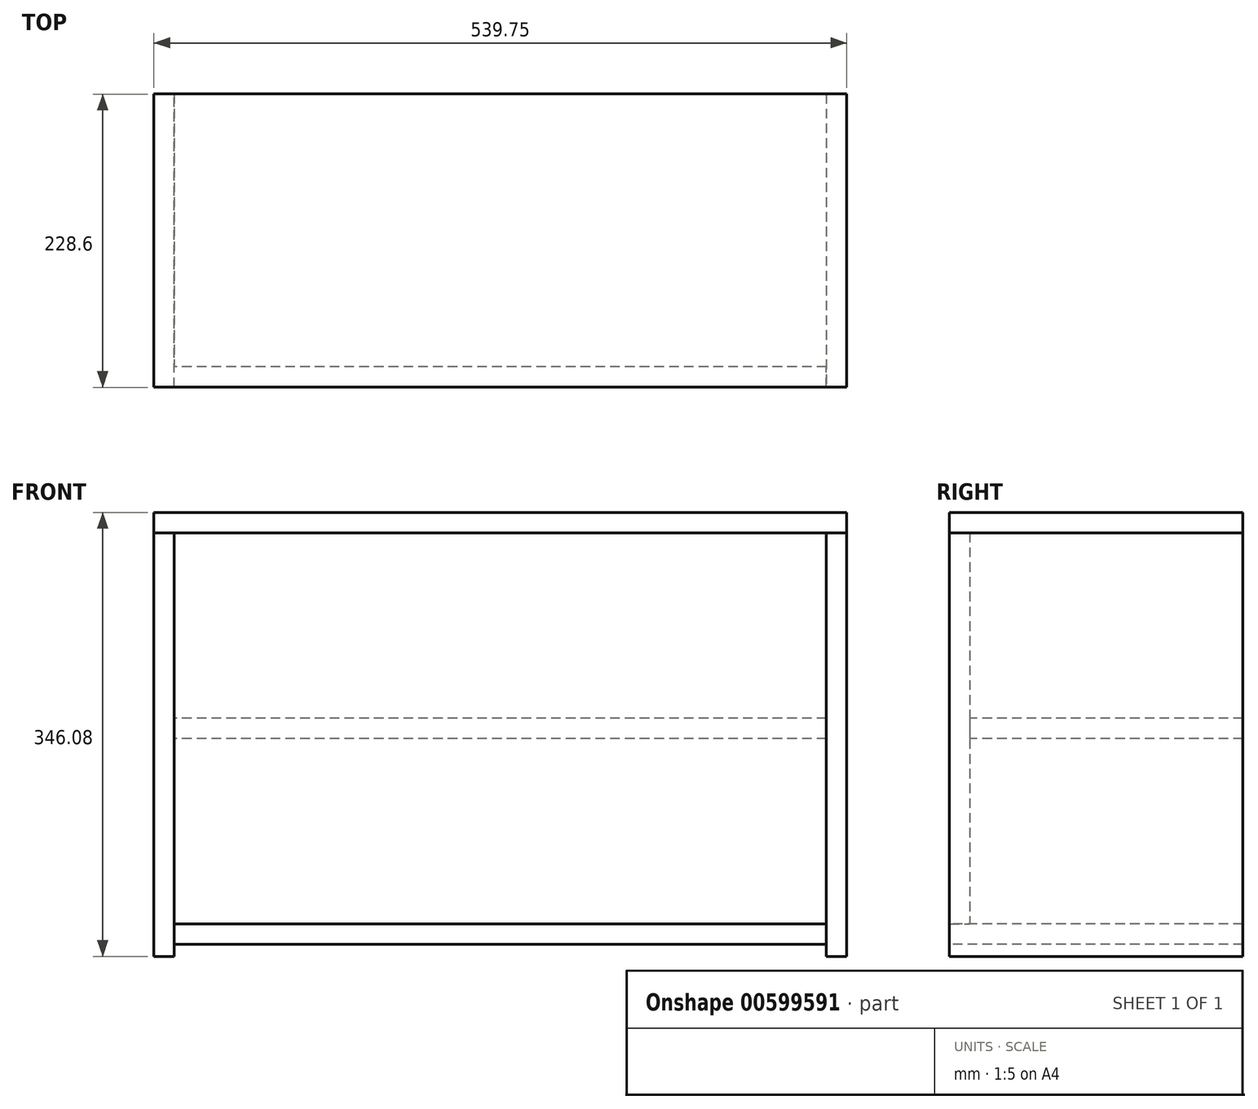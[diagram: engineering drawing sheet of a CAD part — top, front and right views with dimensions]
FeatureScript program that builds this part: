
annotation { "Feature Type Name" : "Feature", "Feature Type Description" : "" }
export const myFeature = defineFeature(function(context is Context, id is Id, definition is map)
    precondition{}
    {
        {
            var Q0;
            Q0=qCreatedBy(makeId("Front.planeOp"),FACE);
            var sketch = newSketch(context, id + "F0", { "sketchPlane" : qUnion([Q0])});
            skLineSegment(sketch, "E0.bottom", {"start": v(-62.15, 287.23) * mm, "end": v(445.85, 287.23) * mm});
            skLineSegment(sketch, "E0.top", {"start": v(-62.15, -17.57) * mm, "end": v(445.85, -17.57) * mm});
            skLineSegment(sketch, "E0.left", {"start": v(-62.15, 287.23) * mm, "end": v(-62.15, -17.57) * mm});
            skLineSegment(sketch, "E0.right", {"start": v(445.85, 287.23) * mm, "end": v(445.85, -17.57) * mm});
            skSolve(sketch);
        }
        {
            var Q0;
            Q0=makeQuery(id+"F0.imprint","IMPRINT",FACE,{"disambiguationData":[TD([[makeQuery(id+"F0.imprint","IMPRINT",EDGE,{"derivedFrom":sQuery(id+"F0.wireOp",EDGE,"E0.bottom")}),-1.0]])]});
            extrude(context, id + "F1", {"entities" : qUnion([Q0]), "depth" : 15.88 * mm, "offsetDistance" : 25.4 * mm});
        }
        {
            var Q0;
            Q0=makeQuery(id+"F1.opExtrude","SWEPT_FACE",FACE,{"disambiguationData":[OSD([sQuery(id+"F0.wireOp",EDGE,"E0.right")])]});
            var sketch = newSketch(context, id + "F2", { "sketchPlane" : qUnion([Q0])});
            skLineSegment(sketch, "E1.bottom", {"start": v(-15.88, 287.23) * mm, "end": v(212.73, 287.23) * mm});
            skLineSegment(sketch, "E1.top", {"start": v(-15.87, -42.97) * mm, "end": v(212.73, -42.97) * mm});
            skLineSegment(sketch, "E1.left", {"start": v(-15.87, 287.23) * mm, "end": v(-15.87, -42.97) * mm});
            skLineSegment(sketch, "E1.right", {"start": v(212.73, 287.23) * mm, "end": v(212.73, -42.97) * mm});
            skSolve(sketch);
        }
        {
            var Q0;
            {var subQ3=sQuery(id+"F2.wireOp",EDGE,"E1.top");Q0=makeQuery(id+"F2.imprint","IMPRINT",FACE,{"disambiguationData":[TD([[makeQuery(id+"F2.imprint","IMPRINT",EDGE,{"derivedFrom":subQ3}),1.0]])]});}
            var Q1;
            {var subQ1=sQuery(id+"F0.wireOp",EDGE,"E0.right");var subQ2=makeQuery(id+"F1.opExtrude","CAP_EDGE",EDGE,{"disambiguationData":[OSD([subQ1])],"isStart":true});Q1=makeQuery(id+"F2.imprint","IMPRINT",FACE,{"disambiguationData":[TD([[makeQuery(id+"F2.imprint","IMPRINT",EDGE,{"derivedFrom":subQ2}),-1.0]])]});}
            extrude(context, id + "F3", {"entities" : qUnion([Q0, Q1]), "depth" : 15.88 * mm, "offsetDistance" : 25.4 * mm});
        }
        {
            var Q0;
            Q0=makeQuery(id+"F1.opExtrude","CAP_EDGE",EDGE,{"disambiguationData":[OSD([sQuery(id+"F0.wireOp",EDGE,"E0.bottom")])],"isStart":false});
            cPoint(context, id + "F4", {"entities" : qUnion([Q0]), "parameter" : 0.5});
        }
        {
            var Q0;
            Q0=makeQuery(id+"F1.opExtrude","CAP_EDGE",EDGE,{"disambiguationData":[OSD([sQuery(id+"F0.wireOp",EDGE,"E0.bottom")])],"isStart":true});
            cPoint(context, id + "F5", {"entities" : qUnion([Q0]), "parameter" : 0.5});
        }
        {
            var Q0;
            Q0=makeQuery(id+"F1.opExtrude","CAP_EDGE",EDGE,{"disambiguationData":[OSD([sQuery(id+"F0.wireOp",EDGE,"E0.top")])],"isStart":false});
            cPoint(context, id + "F6", {"entities" : qUnion([Q0]), "parameter" : 0.5});
        }
        {
            var Q0;
            Q0 = qCreatedBy(id + "F4" ,VERTEX);
            var Q1;
            Q1 = qCreatedBy(id + "F5" ,VERTEX);
            var Q2;
            Q2 = qCreatedBy(id + "F6" ,VERTEX);
            cPlane(context, id + "F7", {"entities" : qUnion([Q0, Q1, Q2]), "cplaneType" : CPlaneType.THREE_POINT, "offset" : 25.4 * mm, "width" : 152.4 * mm, "height" : 152.4 * mm});
        }
        {
            var Q0;
            Q0=makeQuery(id+"F3.opExtrude","SWEPT_BODY",BODY,{"disambiguationData":[OSD([sQuery(id+"F0.wireOp",EDGE,"E0.top"),sQuery(id+"F0.wireOp",EDGE,"E0.right"),sQuery(id+"F2.wireOp",EDGE,"E1.bottom"),sQuery(id+"F2.wireOp",EDGE,"E1.top"),sQuery(id+"F2.wireOp",EDGE,"E1.left"),sQuery(id+"F2.wireOp",EDGE,"E1.right")])]});
            var Q1;
            Q1=qCreatedBy(id+"F7.planeOp",FACE);
            mirror(context, id + "F8", {"entities" : qUnion([Q0]), "mirrorPlane" : qUnion([Q1])});
        }
        {
            var Q0;
            Q0=makeQuery(id+"F8.opPattern","COPY",FACE,{"derivedFrom":makeQuery(id+"F3.opExtrude","SWEPT_FACE",FACE,{"disambiguationData":[OSD([sQuery(id+"F2.wireOp",EDGE,"E1.bottom")])]}),"instanceName":"1"});
            var sketch = newSketch(context, id + "F9", { "sketchPlane" : qUnion([Q0])});
            skLineSegment(sketch, "E2.0", {"start": v(461.73, -15.88) * mm, "end": v(461.73, 212.73) * mm});
            skLineSegment(sketch, "E3", {"start": v(-78.02, 212.73) * mm, "end": v(461.73, 212.73) * mm});
            skLineSegment(sketch, "E4", {"start": v(461.73, -15.88) * mm, "end": v(-78.02, -15.88) * mm});
            skLineSegment(sketch, "E5", {"start": v(-78.02, -15.88) * mm, "end": v(-78.02, 212.73) * mm});
            skSolve(sketch);
        }
        {
            var Q0;
            Q0 = qSketchRegion(id + "F9", true);
            extrude(context, id + "F10", {"entities" : qUnion([Q0]), "depth" : 15.88 * mm, "offsetDistance" : 25.4 * mm});
        }
        {
            var Q0;
            Q0=makeQuery(id+"F1.opExtrude","SWEPT_FACE",FACE,{"disambiguationData":[OSD([sQuery(id+"F0.wireOp",EDGE,"E0.top")])]});
            var sketch = newSketch(context, id + "F11", { "sketchPlane" : qUnion([Q0])});
            skLineSegment(sketch, "E6.0", {"start": v(-78.02, -212.73) * mm, "end": v(461.73, -212.73) * mm});
            skLineSegment(sketch, "E7", {"start": v(-62.15, 15.88) * mm, "end": v(-62.15, -212.73) * mm});
            skLineSegment(sketch, "E8", {"start": v(445.85, -212.73) * mm, "end": v(445.85, 15.88) * mm});
            skLineSegment(sketch, "E9", {"start": v(445.85, 15.88) * mm, "end": v(-62.15, 15.88) * mm});
            skSolve(sketch);
        }
        {
            var Q0;
            Q0 = qSketchRegion(id + "F11", true);
            extrude(context, id + "F12", {"entities" : qUnion([Q0]), "depth" : 15.88 * mm, "offsetDistance" : 25.4 * mm});
        }
        {
            var Q0;
            Q0=makeQuery(id+"F1.opExtrude","CAP_FACE",FACE,{"disambiguationData":[OSD([sQuery(id+"F0.wireOp",EDGE,"E0.bottom"),sQuery(id+"F0.wireOp",EDGE,"E0.top"),sQuery(id+"F0.wireOp",EDGE,"E0.left"),sQuery(id+"F0.wireOp",EDGE,"E0.right")])],"isStart":true});
            var sketch = newSketch(context, id + "F13", { "sketchPlane" : qUnion([Q0])});
            skLineSegment(sketch, "E10.0", {"start": v(62.15, 287.23) * mm, "end": v(62.15, -42.97) * mm, "construction": true});
            skLineSegment(sketch, "E11.0", {"start": v(-445.85, 287.23) * mm, "end": v(-445.85, -42.97) * mm, "construction": true});
            skLineSegment(sketch, "E12", {"start": v(62.15, 134.83) * mm, "end": v(-445.85, 134.83) * mm, "construction": true});
            skLineSegment(sketch, "E13.bottom", {"start": v(-445.85, 126.9) * mm, "end": v(62.15, 126.9) * mm});
            skLineSegment(sketch, "E13.top", {"start": v(-445.85, 142.77) * mm, "end": v(62.15, 142.77) * mm});
            skLineSegment(sketch, "E13.left", {"start": v(-445.85, 126.9) * mm, "end": v(-445.85, 142.77) * mm});
            skLineSegment(sketch, "E13.right", {"start": v(62.15, 126.9) * mm, "end": v(62.15, 142.77) * mm});
            skPoint(sketch, "E14", {"position": v(-445.85, 134.83) * mm});
            skSolve(sketch);
        }
        {
            var Q0;
            Q0=makeQuery(id+"F13.imprint","IMPRINT",FACE,{"disambiguationData":[TD([[makeQuery(id+"F13.imprint","IMPRINT",EDGE,{"derivedFrom":sQuery(id+"F13.wireOp",EDGE,"E13.bottom")}),1.0]])]});
            var Q1;
            Q1=makeQuery(id+"F3.opExtrude","SWEPT_FACE",FACE,{"disambiguationData":[OSD([sQuery(id+"F2.wireOp",EDGE,"E1.right")])]});
            extrude(context, id + "F14", {"entities" : qUnion([Q0]), "endBound" : BoundingType.UP_TO_SURFACE, "depth" : 25.4 * mm, "endBoundEntityFace" : qUnion([Q1]), "offsetDistance" : 25.4 * mm});
        }
    });
